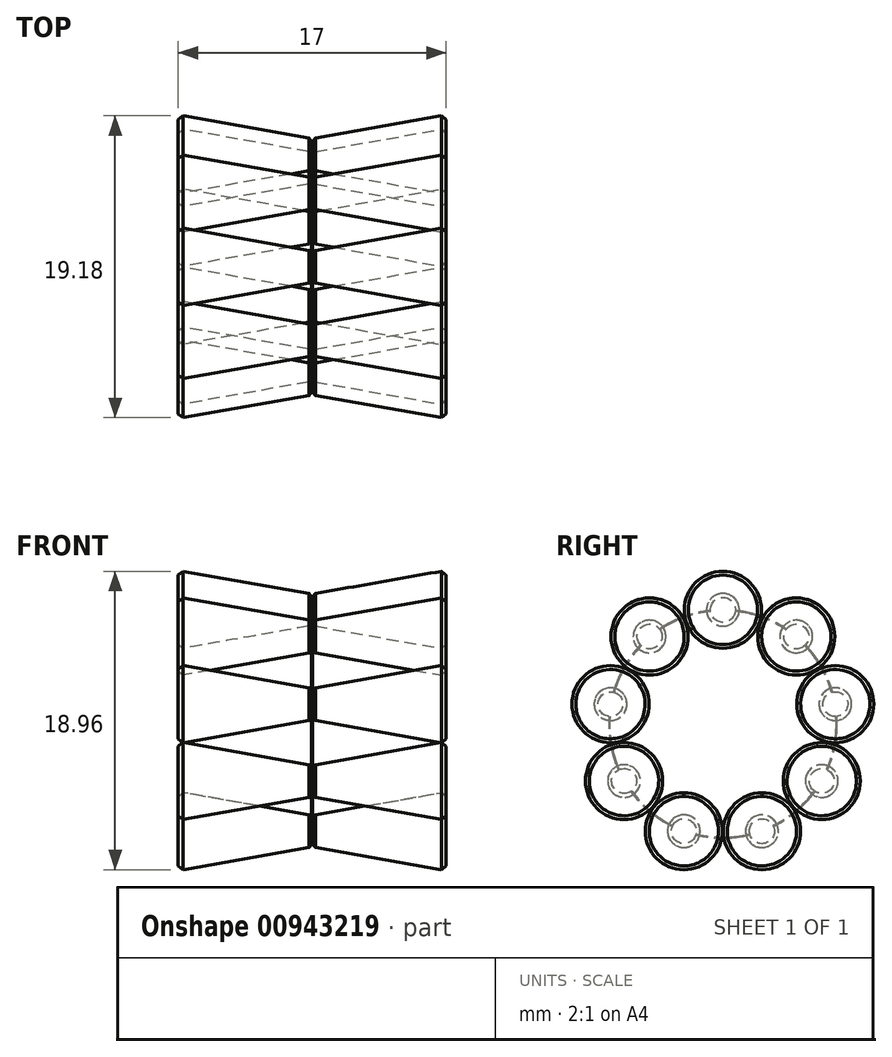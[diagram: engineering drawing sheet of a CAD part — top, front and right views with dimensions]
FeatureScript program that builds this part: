
annotation { "Feature Type Name" : "Feature", "Feature Type Description" : "" }
export const myFeature = defineFeature(function(context is Context, id is Id, definition is map)
    precondition{}
    {
        {
            var Q0;
            Q0=qCreatedBy(makeId("Top.planeOp"),FACE);
            var sketch = newSketch(context, id + "F0", { "sketchPlane" : qUnion([Q0])});
            skLineSegment(sketch, "E0", {"start": v(-8.5, 2.5) * mm, "end": v(-8.5, 0) * mm});
            skLineSegment(sketch, "E1", {"start": v(-8.5, 0) * mm, "end": v(0, 0) * mm});
            skLineSegment(sketch, "E2", {"start": v(0, 0) * mm, "end": v(0, 1) * mm});
            skLineSegment(sketch, "E3", {"start": v(0, 1) * mm, "end": v(-8.5, 2.5) * mm});
            skLineSegment(sketch, "E4", {"start": v(-55.75, 0) * mm, "end": v(47.18, 0) * mm});
            skLineSegment(sketch, "E5", {"start": v(0, 1) * mm, "end": v(8.5, 2.5) * mm});
            skLineSegment(sketch, "E6", {"start": v(8.5, 2.5) * mm, "end": v(8.5, 0) * mm});
            skLineSegment(sketch, "E7", {"start": v(8.5, 0) * mm, "end": v(0, 0) * mm});
            skSolve(sketch);
        }
        {
            var Q0;
            {var subQ0=sQuery(id+"F0.wireOp",EDGE,"E0");Q0=makeQuery(id+"F0.imprint","IMPRINT",FACE,{"disambiguationData":[TD([[makeQuery(id+"F0.imprint","IMPRINT",EDGE,{"derivedFrom":subQ0}),1.0]])]});}
            var Q1;
            Q1=makeQuery(id+"F0.imprint","IMPRINT",FACE,{"disambiguationData":[TD([[makeQuery(id+"F0.imprint","IMPRINT",EDGE,{"derivedFrom":sQuery(id+"F0.wireOp",EDGE,"E2")}),-1.0]])]});
            var Q2;
            Q2=sQuery(id+"F0.wireOp",EDGE,"E4");
            revolve(context, id + "F1", {"surfaceOperationType" : NewSurfaceOperationType.NEW, "entities" : qUnion([Q0, Q1]), "axis" : qUnion([Q2]), "revolveType" : RevolveType.FULL});
        }
        {
            var Q0;
            Q0=makeQuery(id+"F1.opRevolve","SWEPT_EDGE",EDGE,{"disambiguationData":[OSD([sQuery(id+"F0.wireOp",EDGE,"E2"),sQuery(id+"F0.wireOp",EDGE,"E3")])]});
            var Q1;
            Q1=makeQuery(id+"F1.opRevolve","SWEPT_FACE",FACE,{"disambiguationData":[OSD([sQuery(id+"F0.wireOp",EDGE,"E5")])]});
            var Q2;
            Q2=makeQuery(id+"F1.opRevolve","SWEPT_EDGE",EDGE,{"disambiguationData":[OSD([sQuery(id+"F0.wireOp",EDGE,"E0"),sQuery(id+"F0.wireOp",EDGE,"E3")])]});
            chamfer(context, id + "F2", {"entities" : qUnion([Q0, Q1, Q2]), "width" : .25 * mm, "tangentPropagation" : true});
        }
        {
            var Q0;
            Q0=makeQuery(id+"F1.opRevolve","SWEPT_BODY",BODY,{"disambiguationData":[OSD([sQuery(id+"F0.wireOp",EDGE,"E0"),sQuery(id+"F0.wireOp",EDGE,"E2"),sQuery(id+"F0.wireOp",EDGE,"E3"),sQuery(id+"F0.wireOp",EDGE,"E4")])]});
            var Q1;
            Q1=makeQuery(id+"F1.opRevolve","SWEPT_BODY",BODY,{"disambiguationData":[OSD([sQuery(id+"F0.wireOp",EDGE,"E2"),sQuery(id+"F0.wireOp",EDGE,"E5"),sQuery(id+"F0.wireOp",EDGE,"E6"),sQuery(id+"F0.wireOp",EDGE,"E7")])]});
            transform(context, id + "F3", {"entities" : qUnion([Q0, Q1]), "transformType" : TransformType.TRANSLATION_3D, "dx" : 0 * mm, "dy" : 0 * mm, "dz" : (12.5 + 2) / 2 * mm, "makeCopy" : false});
        }
        {
            var Q0;
            Q0=makeQuery(id+"F1.opRevolve","SWEPT_BODY",BODY,{"disambiguationData":[OSD([sQuery(id+"F0.wireOp",EDGE,"E2"),sQuery(id+"F0.wireOp",EDGE,"E5"),sQuery(id+"F0.wireOp",EDGE,"E6"),sQuery(id+"F0.wireOp",EDGE,"E7")])]});
            var Q1;
            Q1=makeQuery(id+"F1.opRevolve","SWEPT_BODY",BODY,{"disambiguationData":[OSD([sQuery(id+"F0.wireOp",EDGE,"E0"),sQuery(id+"F0.wireOp",EDGE,"E2"),sQuery(id+"F0.wireOp",EDGE,"E3"),sQuery(id+"F0.wireOp",EDGE,"E4")])]});
            var Q2;
            Q2=sQuery(id+"F0.wireOp",EDGE,"E4");
            circularPattern(context, id + "F4", {"entities" : qUnion([Q0, Q1]), "axis" : qUnion([Q2]), "angle" : 360 * degree, "instanceCount" : 9, "equalSpace" : true});
        }
        {
            var Q0;
            Q0=qCreatedBy(makeId("Right.planeOp"),FACE);
            var sketch = newSketch(context, id + "F5", { "sketchPlane" : qUnion([Q0])});
            skCircle(sketch, "E8", {"center": v(0, 0) * mm, "radius": 7.2 * mm});
            skCircle(sketch, "E9", {"center": v(0, 0) * mm, "radius": 7.25 * mm});
            skSolve(sketch);
        }
        {
            var Q0;
            Q0=qSketchRegion(id+"F5",true);
            extrude(context, id + "F6", {"entities" : qUnion([Q0]), "operationType" : NewBodyOperationType.ADD, "depth" : 0.05 * mm, "offsetDistance" : 25 * mm, "symmetric" : true});
        }
    });
